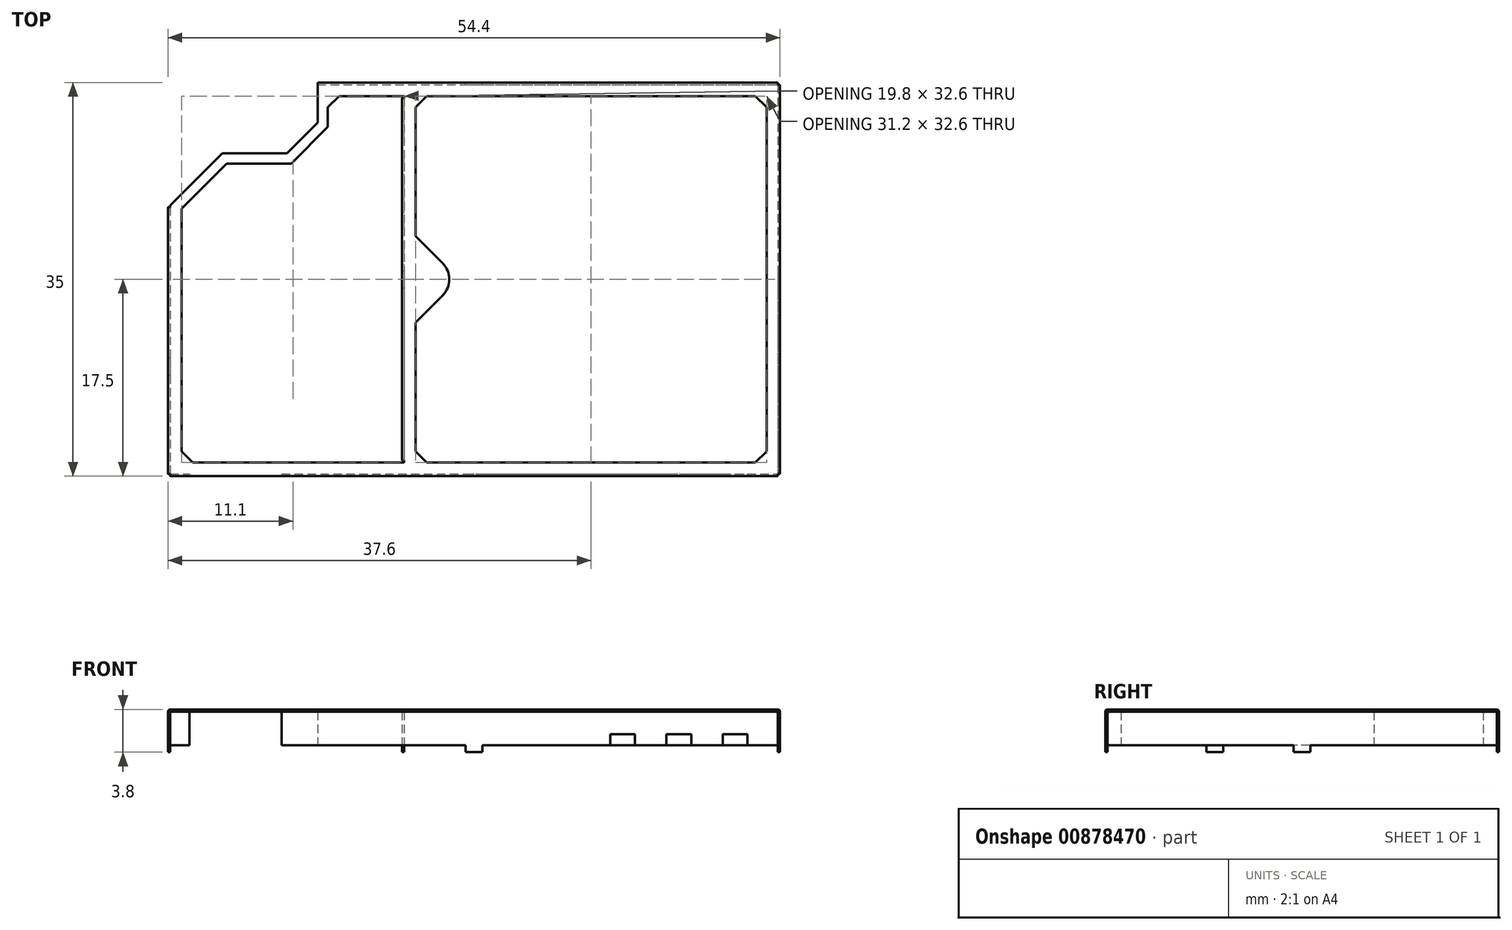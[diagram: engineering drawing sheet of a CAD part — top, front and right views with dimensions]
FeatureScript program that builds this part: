
annotation { "Feature Type Name" : "Feature", "Feature Type Description" : "" }
export const myFeature = defineFeature(function(context is Context, id is Id, definition is map)
    precondition{}
    {
        {
            var Q0;
            Q0=qCreatedBy(makeId("Top.planeOp"),FACE);
            var sketch = newSketch(context, id + "F0", { "sketchPlane" : qUnion([Q0])});
            skLineSegment(sketch, "E0", {"start": v(-26.5, 6.4) * mm, "end": v(-26.5, -17.3) * mm});
            skLineSegment(sketch, "E1", {"start": v(-26.3, -17.5) * mm, "end": v(27.7, -17.5) * mm});
            skLineSegment(sketch, "E2", {"start": v(-26.3, -17.3) * mm, "end": v(-26.5, -17.3) * mm});
            skLineSegment(sketch, "E3", {"start": v(-26.3, -17.3) * mm, "end": v(-26.3, -17.5) * mm});
            skLineSegment(sketch, "E4", {"start": v(27.7, -17.5) * mm, "end": v(27.7, -17.3) * mm});
            skLineSegment(sketch, "E5", {"start": v(27.7, -17.3) * mm, "end": v(27.9, -17.3) * mm});
            skLineSegment(sketch, "E6", {"start": v(27.7, 17.3) * mm, "end": v(27.7, 17.5) * mm});
            skLineSegment(sketch, "E7", {"start": v(27.9, 17.3) * mm, "end": v(27.7, 17.3) * mm});
            skLineSegment(sketch, "E8", {"start": v(27.9, 17.3) * mm, "end": v(27.9, -17.3) * mm});
            skLineSegment(sketch, "E9", {"start": v(-13.2, 17.5) * mm, "end": v(27.7, 17.5) * mm});
            skLineSegment(sketch, "E10", {"start": v(-26.5, 6.4) * mm, "end": v(-26.3, 6.4) * mm});
            skLineSegment(sketch, "E11", {"start": v(-26.3, 6.5) * mm, "end": v(-26.3, 6.56) * mm});
            skLineSegment(sketch, "E12", {"start": v(-25.3, 6.29) * mm, "end": v(-25.3, -15.3) * mm});
            skLineSegment(sketch, "E13", {"start": v(-24.3, -16.3) * mm, "end": v(-5.5, -16.3) * mm});
            skLineSegment(sketch, "E14", {"start": v(26.7, 15.3) * mm, "end": v(26.7, -15.3) * mm});
            skLineSegment(sketch, "E15", {"start": v(-11.3, 16.3) * mm, "end": v(-5.5, 16.3) * mm});
            skLineSegment(sketch, "E16", {"start": v(-5.7, 16.1) * mm, "end": v(-5.7, -16.1) * mm});
            skLineSegment(sketch, "E17", {"start": v(-3.5, 16.3) * mm, "end": v(25.7, 16.3) * mm});
            skLineSegment(sketch, "E18", {"start": v(-3.5, -16.3) * mm, "end": v(25.7, -16.3) * mm});
            skLineSegment(sketch, "E19", {"start": v(-5.7, -16.1) * mm, "end": v(-5.5, -16.1) * mm});
            skLineSegment(sketch, "E20", {"start": v(-5.5, -16.1) * mm, "end": v(-5.5, -16.3) * mm});
            skLineSegment(sketch, "E21", {"start": v(-25.3, 6.29) * mm, "end": v(-21.29, 10.3) * mm});
            skLineSegment(sketch, "E22", {"start": v(-21.29, 10.3) * mm, "end": v(-15.55, 10.3) * mm});
            skLineSegment(sketch, "E23", {"start": v(-12.3, 13.55) * mm, "end": v(-15.55, 10.3) * mm});
            skLineSegment(sketch, "E24", {"start": v(-12.3, 13.55) * mm, "end": v(-12.3, 15.3) * mm});
            skLineSegment(sketch, "E25", {"start": v(-5.7, 16.1) * mm, "end": v(-5.5, 16.1) * mm});
            skLineSegment(sketch, "E26", {"start": v(-5.5, 16.1) * mm, "end": v(-5.5, 16.3) * mm});
            skLineSegment(sketch, "E27", {"start": v(-26.3, 6.5) * mm, "end": v(-26.3, -17.3) * mm});
            skLineSegment(sketch, "E28", {"start": v(-26.3, -17.3) * mm, "end": v(-24.6, -17.3) * mm});
            skLineSegment(sketch, "E29", {"start": v(-5.5, 16.1) * mm, "end": v(-5.5, -16.1) * mm});
            skLineSegment(sketch, "E30", {"start": v(-13.2, 17.3) * mm, "end": v(27.7, 17.3) * mm});
            skLineSegment(sketch, "E31", {"start": v(27.7, 17.3) * mm, "end": v(27.7, -17.3) * mm});
            skLineSegment(sketch, "E32", {"start": v(-24.6, -17.3) * mm, "end": v(-24.6, -17.5) * mm});
            skLineSegment(sketch, "E33", {"start": v(-16.4, -17.3) * mm, "end": v(-16.4, -17.5) * mm});
            skLineSegment(sketch, "E34", {"start": v(-16.4, -17.3) * mm, "end": v(27.7, -17.3) * mm});
            skLineSegment(sketch, "E35", {"start": v(12.8, -17.5) * mm, "end": v(12.8, -17.3) * mm});
            skLineSegment(sketch, "E36", {"start": v(17.8, -17.5) * mm, "end": v(17.8, -17.3) * mm});
            skLineSegment(sketch, "E37", {"start": v(22.8, -17.5) * mm, "end": v(22.8, -17.3) * mm});
            skLineSegment(sketch, "E38", {"start": v(15, -17.5) * mm, "end": v(15, -17.3) * mm});
            skLineSegment(sketch, "E39", {"start": v(20, -17.5) * mm, "end": v(20, -17.3) * mm});
            skLineSegment(sketch, "E40", {"start": v(25, -17.5) * mm, "end": v(25, -17.3) * mm});
            skLineSegment(sketch, "E41", {"start": v(1.45, -17.5) * mm, "end": v(1.45, -17.3) * mm});
            skLineSegment(sketch, "E42", {"start": v(-0.05, -17.5) * mm, "end": v(-0.05, -17.3) * mm});
            skLineSegment(sketch, "E43", {"start": v(1.45, 17.3) * mm, "end": v(1.45, 17.5) * mm});
            skLineSegment(sketch, "E44", {"start": v(-0.05, 17.3) * mm, "end": v(-0.05, 17.5) * mm});
            skLineSegment(sketch, "E45", {"start": v(27.7, 0.75) * mm, "end": v(27.9, 0.75) * mm});
            skLineSegment(sketch, "E46", {"start": v(27.7, -0.75) * mm, "end": v(27.9, -0.75) * mm});
            skLineSegment(sketch, "E47", {"start": v(-5.7, 0.75) * mm, "end": v(-5.5, 0.75) * mm});
            skLineSegment(sketch, "E48", {"start": v(-5.7, -0.75) * mm, "end": v(-5.5, -0.75) * mm});
            skLineSegment(sketch, "E49", {"start": v(-26.3, 6.56) * mm, "end": v(-21.66, 11.2) * mm});
            skLineSegment(sketch, "E50", {"start": v(-21.66, 11.2) * mm, "end": v(-15.93, 11.2) * mm});
            skLineSegment(sketch, "E51", {"start": v(-13.2, 13.93) * mm, "end": v(-15.93, 11.2) * mm});
            skLineSegment(sketch, "E52", {"start": v(-13.2, 13.93) * mm, "end": v(-13.2, 17.5) * mm});
            skLineSegment(sketch, "E53", {"start": v(-26.5, -8.5) * mm, "end": v(-26.3, -8.5) * mm});
            skLineSegment(sketch, "E54", {"start": v(-26.5, -7) * mm, "end": v(-26.3, -7) * mm});
            skLineSegment(sketch, "E55", {"start": v(-2.09, -1.41) * mm, "end": v(-4.5, -3.83) * mm});
            skLineSegment(sketch, "E56", {"start": v(-12.3, 15.3) * mm, "end": v(-11.3, 16.3) * mm});
            skLineSegment(sketch, "E57", {"start": v(-25.3, -15.3) * mm, "end": v(-24.3, -16.3) * mm});
            skLineSegment(sketch, "E58", {"start": v(25.7, -16.3) * mm, "end": v(26.7, -15.3) * mm});
            skLineSegment(sketch, "E59", {"start": v(25.7, 16.3) * mm, "end": v(26.7, 15.3) * mm});
            skLineSegment(sketch, "E60", {"start": v(-4.5, -15.3) * mm, "end": v(-3.5, -16.3) * mm});
            skLineSegment(sketch, "E61", {"start": v(-4.5, 15.3) * mm, "end": v(-3.5, 16.3) * mm});
            skLineSegment(sketch, "E62", {"start": v(-2.09, 1.41) * mm, "end": v(-4.5, 3.83) * mm});
            skArc(sketch, "E63", {"start": v(-2.09, -1.41) * mm, "mid": v(-1.5, 0) * mm, "end": v(-2.09, 1.41) * mm});
            skLineSegment(sketch, "E64", {"start": v(-4.5, -3.83) * mm, "end": v(-4.5, -15.3) * mm});
            skLineSegment(sketch, "E65", {"start": v(-4.5, 15.3) * mm, "end": v(-4.5, 3.83) * mm});
            skLineSegment(sketch, "E66", {"start": v(-26.3, 6.4) * mm, "end": v(-26.3, 6.56) * mm});
            skSolve(sketch);
        }
        {
            var Q0;
            {var subQ0=sQuery(id+"F0.wireOp",EDGE,"E53");Q0=makeQuery(id+"F0.imprint","IMPRINT",FACE,{"disambiguationData":[TD([[makeQuery(id+"F0.imprint","IMPRINT",EDGE,{"derivedFrom":subQ0}),1.0]])]});}
            var Q1;
            {var subQ0=sQuery(id+"F0.wireOp",EDGE,"E10");Q1=makeQuery(id+"F0.imprint","IMPRINT",FACE,{"disambiguationData":[TD([[makeQuery(id+"F0.imprint","IMPRINT",EDGE,{"derivedFrom":subQ0}),-1.0]])]});}
            var Q2;
            {var subQ0=sQuery(id+"F0.wireOp",EDGE,"E2");Q2=makeQuery(id+"F0.imprint","IMPRINT",FACE,{"disambiguationData":[TD([[makeQuery(id+"F0.imprint","IMPRINT",EDGE,{"derivedFrom":subQ0}),-1.0]])]});}
            var Q3;
            {var subQ0=sQuery(id+"F0.wireOp",EDGE,"E3");Q3=makeQuery(id+"F0.imprint","IMPRINT",FACE,{"disambiguationData":[TD([[makeQuery(id+"F0.imprint","IMPRINT",EDGE,{"derivedFrom":subQ0}),1.0]])]});}
            var Q4;
            {var subQ0=sQuery(id+"F0.wireOp",EDGE,"E33");Q4=makeQuery(id+"F0.imprint","IMPRINT",FACE,{"disambiguationData":[TD([[makeQuery(id+"F0.imprint","IMPRINT",EDGE,{"derivedFrom":subQ0}),1.0]])]});}
            var Q5;
            {var subQ0=sQuery(id+"F0.wireOp",EDGE,"E19");Q5=makeQuery(id+"F0.imprint","IMPRINT",FACE,{"disambiguationData":[TD([[makeQuery(id+"F0.imprint","IMPRINT",EDGE,{"derivedFrom":subQ0}),1.0]])]});}
            var Q6;
            {var subQ0=sQuery(id+"F0.wireOp",EDGE,"E41");Q6=makeQuery(id+"F0.imprint","IMPRINT",FACE,{"disambiguationData":[TD([[makeQuery(id+"F0.imprint","IMPRINT",EDGE,{"derivedFrom":subQ0}),1.0]])]});}
            var Q7;
            {var subQ0=sQuery(id+"F0.wireOp",EDGE,"E35");Q7=makeQuery(id+"F0.imprint","IMPRINT",FACE,{"disambiguationData":[TD([[makeQuery(id+"F0.imprint","IMPRINT",EDGE,{"derivedFrom":subQ0}),1.0]])]});}
            var Q8;
            {var subQ0=sQuery(id+"F0.wireOp",EDGE,"E35");Q8=makeQuery(id+"F0.imprint","IMPRINT",FACE,{"disambiguationData":[TD([[makeQuery(id+"F0.imprint","IMPRINT",EDGE,{"derivedFrom":subQ0}),-1.0]])]});}
            var Q9;
            {var subQ0=sQuery(id+"F0.wireOp",EDGE,"E36");Q9=makeQuery(id+"F0.imprint","IMPRINT",FACE,{"disambiguationData":[TD([[makeQuery(id+"F0.imprint","IMPRINT",EDGE,{"derivedFrom":subQ0}),1.0]])]});}
            var Q10;
            {var subQ0=sQuery(id+"F0.wireOp",EDGE,"E36");Q10=makeQuery(id+"F0.imprint","IMPRINT",FACE,{"disambiguationData":[TD([[makeQuery(id+"F0.imprint","IMPRINT",EDGE,{"derivedFrom":subQ0}),-1.0]])]});}
            var Q11;
            {var subQ0=sQuery(id+"F0.wireOp",EDGE,"E37");Q11=makeQuery(id+"F0.imprint","IMPRINT",FACE,{"disambiguationData":[TD([[makeQuery(id+"F0.imprint","IMPRINT",EDGE,{"derivedFrom":subQ0}),1.0]])]});}
            var Q12;
            {var subQ0=sQuery(id+"F0.wireOp",EDGE,"E37");Q12=makeQuery(id+"F0.imprint","IMPRINT",FACE,{"disambiguationData":[TD([[makeQuery(id+"F0.imprint","IMPRINT",EDGE,{"derivedFrom":subQ0}),-1.0]])]});}
            var Q13;
            {var subQ0=sQuery(id+"F0.wireOp",EDGE,"E4");Q13=makeQuery(id+"F0.imprint","IMPRINT",FACE,{"disambiguationData":[TD([[makeQuery(id+"F0.imprint","IMPRINT",EDGE,{"derivedFrom":subQ0}),1.0]])]});}
            var Q14;
            {var subQ0=sQuery(id+"F0.wireOp",EDGE,"E5");Q14=makeQuery(id+"F0.imprint","IMPRINT",FACE,{"disambiguationData":[TD([[makeQuery(id+"F0.imprint","IMPRINT",EDGE,{"derivedFrom":subQ0}),1.0]])]});}
            var Q15;
            {var subQ0=sQuery(id+"F0.wireOp",EDGE,"E45");Q15=makeQuery(id+"F0.imprint","IMPRINT",FACE,{"disambiguationData":[TD([[makeQuery(id+"F0.imprint","IMPRINT",EDGE,{"derivedFrom":subQ0}),-1.0]])]});}
            var Q16;
            {var subQ0=sQuery(id+"F0.wireOp",EDGE,"E7");Q16=makeQuery(id+"F0.imprint","IMPRINT",FACE,{"disambiguationData":[TD([[makeQuery(id+"F0.imprint","IMPRINT",EDGE,{"derivedFrom":subQ0}),1.0]])]});}
            var Q17;
            {var subQ0=sQuery(id+"F0.wireOp",EDGE,"E6");Q17=makeQuery(id+"F0.imprint","IMPRINT",FACE,{"disambiguationData":[TD([[makeQuery(id+"F0.imprint","IMPRINT",EDGE,{"derivedFrom":subQ0}),1.0]])]});}
            var Q18;
            {var subQ0=sQuery(id+"F0.wireOp",EDGE,"E47");Q18=makeQuery(id+"F0.imprint","IMPRINT",FACE,{"disambiguationData":[TD([[makeQuery(id+"F0.imprint","IMPRINT",EDGE,{"derivedFrom":subQ0}),-1.0]])]});}
            var Q19;
            {var subQ0=sQuery(id+"F0.wireOp",EDGE,"E25");Q19=makeQuery(id+"F0.imprint","IMPRINT",FACE,{"disambiguationData":[TD([[makeQuery(id+"F0.imprint","IMPRINT",EDGE,{"derivedFrom":subQ0}),-1.0]])]});}
            var Q20;
            {var subQ0=sQuery(id+"F0.wireOp",EDGE,"E43");Q20=makeQuery(id+"F0.imprint","IMPRINT",FACE,{"disambiguationData":[TD([[makeQuery(id+"F0.imprint","IMPRINT",EDGE,{"derivedFrom":subQ0}),1.0]])]});}
            var Q21;
            {var subQ3=sQuery(id+"F0.wireOp",EDGE,"E44");Q21=makeQuery(id+"F0.imprint","IMPRINT",FACE,{"disambiguationData":[TD([[makeQuery(id+"F0.imprint","IMPRINT",EDGE,{"derivedFrom":subQ3}),1.0]])]});}
            extrude(context, id + "F1", {"entities" : qUnion([Q0, Q1, Q2, Q3, Q4, Q5, Q6, Q7, Q8, Q9, Q10, Q11, Q12, Q13, Q14, Q15, Q16, Q17, Q18, Q19, Q20, Q21]), "depth" : 3 * mm, "offsetDistance" : 25 * mm});
        }
        {
            var Q0;
            Q0=makeQuery(id+"F0.imprint","IMPRINT",FACE,{"disambiguationData":[TD([[makeQuery(id+"F0.imprint","IMPRINT",EDGE,{"derivedFrom":sQuery(id+"F0.wireOp",EDGE,"E12")}),-1.0]])]});
            var Q1;
            {var subQ0=sQuery(id+"F0.wireOp",EDGE,"E3");Q1=makeQuery(id+"F0.imprint","IMPRINT",FACE,{"disambiguationData":[TD([[makeQuery(id+"F0.imprint","IMPRINT",EDGE,{"derivedFrom":subQ0}),1.0]])]});}
            var Q2;
            {var subQ0=sQuery(id+"F0.wireOp",EDGE,"E2");Q2=makeQuery(id+"F0.imprint","IMPRINT",FACE,{"disambiguationData":[TD([[makeQuery(id+"F0.imprint","IMPRINT",EDGE,{"derivedFrom":subQ0}),-1.0]])]});}
            var Q3;
            {var subQ0=sQuery(id+"F0.wireOp",EDGE,"E53");Q3=makeQuery(id+"F0.imprint","IMPRINT",FACE,{"disambiguationData":[TD([[makeQuery(id+"F0.imprint","IMPRINT",EDGE,{"derivedFrom":subQ0}),1.0]])]});}
            var Q4;
            {var subQ0=sQuery(id+"F0.wireOp",EDGE,"E10");Q4=makeQuery(id+"F0.imprint","IMPRINT",FACE,{"disambiguationData":[TD([[makeQuery(id+"F0.imprint","IMPRINT",EDGE,{"derivedFrom":subQ0}),-1.0]])]});}
            var Q5;
            {var subQ3=sQuery(id+"F0.wireOp",EDGE,"E44");Q5=makeQuery(id+"F0.imprint","IMPRINT",FACE,{"disambiguationData":[TD([[makeQuery(id+"F0.imprint","IMPRINT",EDGE,{"derivedFrom":subQ3}),1.0]])]});}
            var Q6;
            {var subQ0=sQuery(id+"F0.wireOp",EDGE,"E25");Q6=makeQuery(id+"F0.imprint","IMPRINT",FACE,{"disambiguationData":[TD([[makeQuery(id+"F0.imprint","IMPRINT",EDGE,{"derivedFrom":subQ0}),-1.0]])]});}
            var Q7;
            {var subQ0=sQuery(id+"F0.wireOp",EDGE,"E47");Q7=makeQuery(id+"F0.imprint","IMPRINT",FACE,{"disambiguationData":[TD([[makeQuery(id+"F0.imprint","IMPRINT",EDGE,{"derivedFrom":subQ0}),-1.0]])]});}
            var Q8;
            {var subQ0=sQuery(id+"F0.wireOp",EDGE,"E19");Q8=makeQuery(id+"F0.imprint","IMPRINT",FACE,{"disambiguationData":[TD([[makeQuery(id+"F0.imprint","IMPRINT",EDGE,{"derivedFrom":subQ0}),1.0]])]});}
            var Q9;
            {var subQ0=sQuery(id+"F0.wireOp",EDGE,"E33");Q9=makeQuery(id+"F0.imprint","IMPRINT",FACE,{"disambiguationData":[TD([[makeQuery(id+"F0.imprint","IMPRINT",EDGE,{"derivedFrom":subQ0}),1.0]])]});}
            var Q10;
            {var subQ0=sQuery(id+"F0.wireOp",EDGE,"E41");Q10=makeQuery(id+"F0.imprint","IMPRINT",FACE,{"disambiguationData":[TD([[makeQuery(id+"F0.imprint","IMPRINT",EDGE,{"derivedFrom":subQ0}),1.0]])]});}
            var Q11;
            {var subQ0=sQuery(id+"F0.wireOp",EDGE,"E35");Q11=makeQuery(id+"F0.imprint","IMPRINT",FACE,{"disambiguationData":[TD([[makeQuery(id+"F0.imprint","IMPRINT",EDGE,{"derivedFrom":subQ0}),1.0]])]});}
            var Q12;
            {var subQ0=sQuery(id+"F0.wireOp",EDGE,"E35");Q12=makeQuery(id+"F0.imprint","IMPRINT",FACE,{"disambiguationData":[TD([[makeQuery(id+"F0.imprint","IMPRINT",EDGE,{"derivedFrom":subQ0}),-1.0]])]});}
            var Q13;
            {var subQ0=sQuery(id+"F0.wireOp",EDGE,"E36");Q13=makeQuery(id+"F0.imprint","IMPRINT",FACE,{"disambiguationData":[TD([[makeQuery(id+"F0.imprint","IMPRINT",EDGE,{"derivedFrom":subQ0}),1.0]])]});}
            var Q14;
            {var subQ0=sQuery(id+"F0.wireOp",EDGE,"E36");Q14=makeQuery(id+"F0.imprint","IMPRINT",FACE,{"disambiguationData":[TD([[makeQuery(id+"F0.imprint","IMPRINT",EDGE,{"derivedFrom":subQ0}),-1.0]])]});}
            var Q15;
            {var subQ0=sQuery(id+"F0.wireOp",EDGE,"E37");Q15=makeQuery(id+"F0.imprint","IMPRINT",FACE,{"disambiguationData":[TD([[makeQuery(id+"F0.imprint","IMPRINT",EDGE,{"derivedFrom":subQ0}),1.0]])]});}
            var Q16;
            {var subQ0=sQuery(id+"F0.wireOp",EDGE,"E37");Q16=makeQuery(id+"F0.imprint","IMPRINT",FACE,{"disambiguationData":[TD([[makeQuery(id+"F0.imprint","IMPRINT",EDGE,{"derivedFrom":subQ0}),-1.0]])]});}
            var Q17;
            {var subQ0=sQuery(id+"F0.wireOp",EDGE,"E4");Q17=makeQuery(id+"F0.imprint","IMPRINT",FACE,{"disambiguationData":[TD([[makeQuery(id+"F0.imprint","IMPRINT",EDGE,{"derivedFrom":subQ0}),1.0]])]});}
            var Q18;
            {var subQ0=sQuery(id+"F0.wireOp",EDGE,"E5");Q18=makeQuery(id+"F0.imprint","IMPRINT",FACE,{"disambiguationData":[TD([[makeQuery(id+"F0.imprint","IMPRINT",EDGE,{"derivedFrom":subQ0}),1.0]])]});}
            var Q19;
            {var subQ0=sQuery(id+"F0.wireOp",EDGE,"E45");Q19=makeQuery(id+"F0.imprint","IMPRINT",FACE,{"disambiguationData":[TD([[makeQuery(id+"F0.imprint","IMPRINT",EDGE,{"derivedFrom":subQ0}),-1.0]])]});}
            var Q20;
            {var subQ0=sQuery(id+"F0.wireOp",EDGE,"E7");Q20=makeQuery(id+"F0.imprint","IMPRINT",FACE,{"disambiguationData":[TD([[makeQuery(id+"F0.imprint","IMPRINT",EDGE,{"derivedFrom":subQ0}),1.0]])]});}
            var Q21;
            {var subQ0=sQuery(id+"F0.wireOp",EDGE,"E6");Q21=makeQuery(id+"F0.imprint","IMPRINT",FACE,{"disambiguationData":[TD([[makeQuery(id+"F0.imprint","IMPRINT",EDGE,{"derivedFrom":subQ0}),1.0]])]});}
            var Q22;
            {var subQ0=sQuery(id+"F0.wireOp",EDGE,"E43");Q22=makeQuery(id+"F0.imprint","IMPRINT",FACE,{"disambiguationData":[TD([[makeQuery(id+"F0.imprint","IMPRINT",EDGE,{"derivedFrom":subQ0}),1.0]])]});}
            extrude(context, id + "F2", {"entities" : qUnion([Q0, Q1, Q2, Q3, Q4, Q5, Q6, Q7, Q8, Q9, Q10, Q11, Q12, Q13, Q14, Q15, Q16, Q17, Q18, Q19, Q20, Q21, Q22]), "depth" : 3.2 * mm, "offsetDistance" : 25 * mm, "hasSecondDirection" : true, "secondDirectionOppositeDirection" : false, "secondDirectionDepth" : 3 * mm});
        }
        {
            var Q0;
            {var subQ0=sQuery(id+"F0.wireOp",EDGE,"E35");Q0=makeQuery(id+"F0.imprint","IMPRINT",FACE,{"disambiguationData":[TD([[makeQuery(id+"F0.imprint","IMPRINT",EDGE,{"derivedFrom":subQ0}),-1.0]])]});}
            var Q1;
            {var subQ0=sQuery(id+"F0.wireOp",EDGE,"E36");Q1=makeQuery(id+"F0.imprint","IMPRINT",FACE,{"disambiguationData":[TD([[makeQuery(id+"F0.imprint","IMPRINT",EDGE,{"derivedFrom":subQ0}),-1.0]])]});}
            var Q2;
            {var subQ0=sQuery(id+"F0.wireOp",EDGE,"E37");Q2=makeQuery(id+"F0.imprint","IMPRINT",FACE,{"disambiguationData":[TD([[makeQuery(id+"F0.imprint","IMPRINT",EDGE,{"derivedFrom":subQ0}),-1.0]])]});}
            extrude(context, id + "F3", {"entities" : qUnion([Q0, Q1, Q2]), "operationType" : NewBodyOperationType.REMOVE, "depth" : 1 * mm, "offsetDistance" : 25 * mm});
        }
        {
            var Q0;
            {var subQ0=sQuery(id+"F0.wireOp",EDGE,"E41");Q0=makeQuery(id+"F0.imprint","IMPRINT",FACE,{"disambiguationData":[TD([[makeQuery(id+"F0.imprint","IMPRINT",EDGE,{"derivedFrom":subQ0}),1.0]])]});}
            var Q1;
            {var subQ0=sQuery(id+"F0.wireOp",EDGE,"E47");Q1=makeQuery(id+"F0.imprint","IMPRINT",FACE,{"disambiguationData":[TD([[makeQuery(id+"F0.imprint","IMPRINT",EDGE,{"derivedFrom":subQ0}),-1.0]])]});}
            var Q2;
            {var subQ0=sQuery(id+"F0.wireOp",EDGE,"E53");Q2=makeQuery(id+"F0.imprint","IMPRINT",FACE,{"disambiguationData":[TD([[makeQuery(id+"F0.imprint","IMPRINT",EDGE,{"derivedFrom":subQ0}),1.0]])]});}
            var Q3;
            {var subQ0=sQuery(id+"F0.wireOp",EDGE,"E43");Q3=makeQuery(id+"F0.imprint","IMPRINT",FACE,{"disambiguationData":[TD([[makeQuery(id+"F0.imprint","IMPRINT",EDGE,{"derivedFrom":subQ0}),1.0]])]});}
            var Q4;
            {var subQ0=sQuery(id+"F0.wireOp",EDGE,"E45");Q4=makeQuery(id+"F0.imprint","IMPRINT",FACE,{"disambiguationData":[TD([[makeQuery(id+"F0.imprint","IMPRINT",EDGE,{"derivedFrom":subQ0}),-1.0]])]});}
            extrude(context, id + "F4", {"entities" : qUnion([Q0, Q1, Q2, Q3, Q4]), "operationType" : NewBodyOperationType.ADD, "oppositeDirection" : true, "depth" : 0.6 * mm, "offsetDistance" : 25 * mm});
        }
        {
            var Q0;
            Q0=makeQuery(id+"F2.opExtrude","CAP_EDGE",EDGE,{"disambiguationData":[OSD([sQuery(id+"F0.wireOp",EDGE,"E1")])],"isStart":false});
            var Q1;
            Q1=makeQuery(id+"F2.opExtrude","CAP_EDGE",EDGE,{"disambiguationData":[OSD([sQuery(id+"F0.wireOp",EDGE,"E8")])],"isStart":false});
            var Q2;
            Q2=makeQuery(id+"F2.opExtrude","CAP_EDGE",EDGE,{"disambiguationData":[OSD([sQuery(id+"F0.wireOp",EDGE,"E9")])],"isStart":false});
            var Q3;
            Q3=makeQuery(id+"F2.opExtrude","CAP_EDGE",EDGE,{"disambiguationData":[OSD([sQuery(id+"F0.wireOp",EDGE,"E0")])],"isStart":false});
            var Q4;
            Q4=makeQuery(id+"F2.opExtrude","CAP_EDGE",EDGE,{"disambiguationData":[OSD([sQuery(id+"F0.wireOp",EDGE,"E16")])],"isStart":false});
            fillet(context, id + "F5", {"entities" : qUnion([Q0, Q1, Q2, Q3, Q4]), "radius" : 0.2 * mm, "tangentPropagation" : true, "allowEdgeOverflow" : false});
        }
    });
